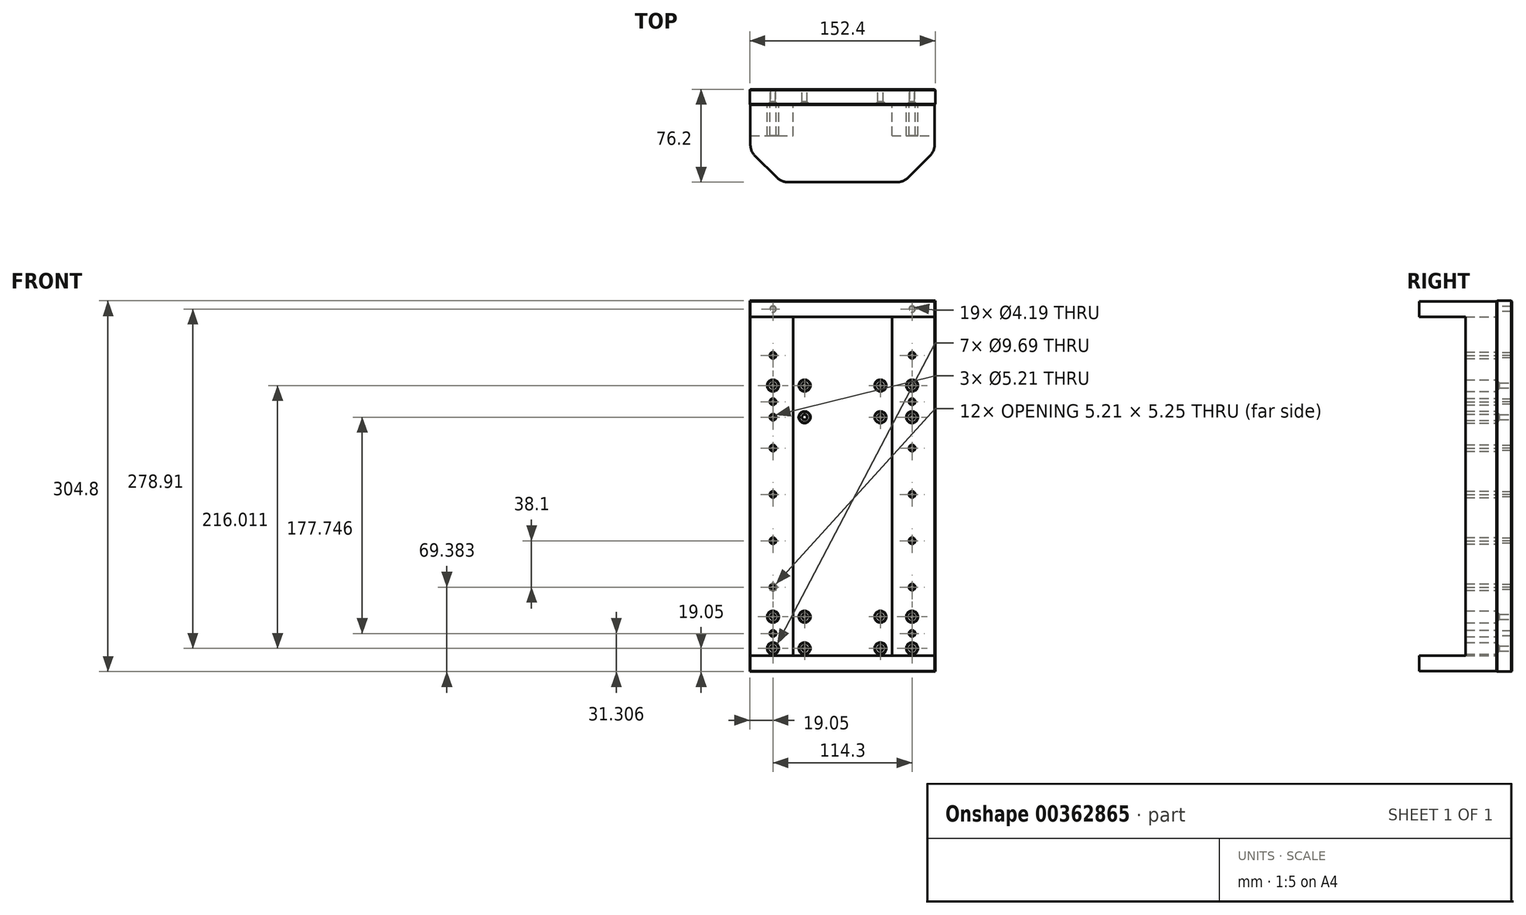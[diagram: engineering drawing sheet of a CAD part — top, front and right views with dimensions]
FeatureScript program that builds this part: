
annotation { "Feature Type Name" : "Feature", "Feature Type Description" : "" }
export const myFeature = defineFeature(function(context is Context, id is Id, definition is map)
    precondition{}
    {
        {
            var Q0;
            Q0=qCreatedBy(makeId("Front.planeOp"),FACE);
            var sketch = newSketch(context, id + "F0", { "sketchPlane" : qUnion([Q0])});
            skLineSegment(sketch, "E0.top", {"start": v(76.2, 152.4) * mm, "end": v(-76.2, 152.4) * mm});
            skLineSegment(sketch, "E0.left", {"start": v(76.2, -152.4) * mm, "end": v(76.2, 152.4) * mm});
            skLineSegment(sketch, "E0.right", {"start": v(-76.2, -152.4) * mm, "end": v(-76.2, 152.4) * mm});
            skPoint(sketch, "E0.middle", {"position": v(0, 0) * mm});
            skCircle(sketch, "E1.MirrorC", {"center": v(31.15, -107.35) * mm, "radius": 2.1 * mm});
            skCircle(sketch, "E2.MirrorC", {"center": v(57.15, -133.35) * mm, "radius": 2.1 * mm});
            skCircle(sketch, "E3.MirrorC", {"center": v(57.15, -107.35) * mm, "radius": 2.1 * mm});
            skCircle(sketch, "E4.MirrorC", {"center": v(31.15, -133.35) * mm, "radius": 2.1 * mm});
            skCircle(sketch, "E5.MirrorC", {"center": v(31.15, 82.66) * mm, "radius": 2.1 * mm});
            skCircle(sketch, "E6.MirrorC", {"center": v(57.15, 56.65) * mm, "radius": 2.1 * mm});
            skCircle(sketch, "E7.MirrorC", {"center": v(57.15, 82.66) * mm, "radius": 2.1 * mm});
            skCircle(sketch, "E8.MirrorC", {"center": v(31.15, 56.65) * mm, "radius": 2.1 * mm});
            skCircle(sketch, "E9.MirrorC", {"center": v(-57.15, -107.35) * mm, "radius": 2.1 * mm});
            skCircle(sketch, "E10.MirrorC", {"center": v(-31.15, -133.35) * mm, "radius": 2.1 * mm});
            skCircle(sketch, "E11.MirrorC", {"center": v(-31.15, -107.35) * mm, "radius": 2.1 * mm});
            skCircle(sketch, "E12.MirrorC", {"center": v(-57.15, -133.35) * mm, "radius": 2.1 * mm});
            skCircle(sketch, "E13.MirrorC", {"center": v(-57.15, 56.65) * mm, "radius": 2.1 * mm});
            skCircle(sketch, "E14.MirrorC", {"center": v(-31.14, 56.65) * mm, "radius": 2.1 * mm});
            skCircle(sketch, "E15.MirrorC", {"center": v(-31.15, 56.65) * mm, "radius": 2.1 * mm});
            skCircle(sketch, "E16.MirrorC", {"center": v(-57.15, 82.66) * mm, "radius": 2.1 * mm});
            skCircle(sketch, "E17.MirrorC", {"center": v(-31.15, 82.66) * mm, "radius": 2.1 * mm});
            skLineSegment(sketch, "E18", {"start": v(-76.2, -152.4) * mm, "end": v(76.2, -152.4) * mm});
            skLineSegment(sketch, "E19", {"start": v(-57.15, -133.35) * mm, "end": v(-57.15, -107.35) * mm, "construction": true});
            skLineSegment(sketch, "E20", {"start": v(-57.15, -120.35) * mm, "end": v(-69.56, -120.35) * mm, "construction": true});
            skPoint(sketch, "E20.endSnap0", {"position": v(-57.15, -120.35) * mm});
            skLineSegment(sketch, "E21", {"start": v(-69.56, -112.82) * mm, "end": v(-69.56, -127.88) * mm, "construction": true});
            skLineSegment(sketch, "E22", {"start": v(-63.35, -120.35) * mm, "end": v(-63.35, 68.86) * mm, "construction": true});
            skSolve(sketch);
        }
        {
            var Q0;
            Q0 = qSketchRegion(id + "F0", true);
            extrude(context, id + "F1", {"entities" : qUnion([Q0]), "depth" : 12.7 * mm});
        }
        {
            var Q0;
            Q0=makeQuery(id+"F1.opExtrude","CAP_EDGE",EDGE,{"disambiguationData":[OSD([sQuery(id+"F0.wireOp",EDGE,"E16.MirrorC")])],"isStart":false});
            var Q1;
            Q1=makeQuery(id+"F1.opExtrude","CAP_EDGE",EDGE,{"disambiguationData":[OSD([sQuery(id+"F0.wireOp",EDGE,"E17.MirrorC")])],"isStart":false});
            var Q2;
            Q2=makeQuery(id+"F1.opExtrude","CAP_EDGE",EDGE,{"disambiguationData":[OSD([sQuery(id+"F0.wireOp",EDGE,"E13.MirrorC")])],"isStart":false});
            var Q3;
            Q3=makeQuery(id+"F1.opExtrude","CAP_EDGE",EDGE,{"disambiguationData":[OSD([sQuery(id+"F0.wireOp",EDGE,"E15.MirrorC")])],"isStart":false});
            var Q4;
            Q4=makeQuery(id+"F1.opExtrude","CAP_EDGE",EDGE,{"disambiguationData":[OSD([sQuery(id+"F0.wireOp",EDGE,"E5.MirrorC")])],"isStart":false});
            var Q5;
            Q5=makeQuery(id+"F1.opExtrude","CAP_EDGE",EDGE,{"disambiguationData":[OSD([sQuery(id+"F0.wireOp",EDGE,"E7.MirrorC")])],"isStart":false});
            var Q6;
            Q6=makeQuery(id+"F1.opExtrude","CAP_EDGE",EDGE,{"disambiguationData":[OSD([sQuery(id+"F0.wireOp",EDGE,"E8.MirrorC")])],"isStart":false});
            var Q7;
            Q7=makeQuery(id+"F1.opExtrude","CAP_EDGE",EDGE,{"disambiguationData":[OSD([sQuery(id+"F0.wireOp",EDGE,"E6.MirrorC")])],"isStart":false});
            var Q8;
            Q8=makeQuery(id+"F1.opExtrude","CAP_EDGE",EDGE,{"disambiguationData":[OSD([sQuery(id+"F0.wireOp",EDGE,"E9.MirrorC")])],"isStart":false});
            var Q9;
            Q9=makeQuery(id+"F1.opExtrude","CAP_EDGE",EDGE,{"disambiguationData":[OSD([sQuery(id+"F0.wireOp",EDGE,"E11.MirrorC")])],"isStart":false});
            var Q10;
            Q10=makeQuery(id+"F1.opExtrude","CAP_EDGE",EDGE,{"disambiguationData":[OSD([sQuery(id+"F0.wireOp",EDGE,"E1.MirrorC")])],"isStart":false});
            var Q11;
            Q11=makeQuery(id+"F1.opExtrude","CAP_EDGE",EDGE,{"disambiguationData":[OSD([sQuery(id+"F0.wireOp",EDGE,"E3.MirrorC")])],"isStart":false});
            var Q12;
            Q12=makeQuery(id+"F1.opExtrude","CAP_EDGE",EDGE,{"disambiguationData":[OSD([sQuery(id+"F0.wireOp",EDGE,"E12.MirrorC")])],"isStart":false});
            var Q13;
            Q13=makeQuery(id+"F1.opExtrude","CAP_EDGE",EDGE,{"disambiguationData":[OSD([sQuery(id+"F0.wireOp",EDGE,"E10.MirrorC")])],"isStart":false});
            var Q14;
            Q14=makeQuery(id+"F1.opExtrude","CAP_EDGE",EDGE,{"disambiguationData":[OSD([sQuery(id+"F0.wireOp",EDGE,"E4.MirrorC")])],"isStart":false});
            var Q15;
            Q15=makeQuery(id+"F1.opExtrude","CAP_EDGE",EDGE,{"disambiguationData":[OSD([sQuery(id+"F0.wireOp",EDGE,"E2.MirrorC")])],"isStart":false});
            chamfer(context, id + "F2", {"entities" : qUnion([Q0, Q1, Q2, Q3, Q4, Q5, Q6, Q7, Q8, Q9, Q10, Q11, Q12, Q13, Q14, Q15]), "width" : 2.54 * mm, "tangentPropagation" : true});
        }
        {
            var Q0;
            Q0=makeQuery(id+"F1.opExtrude","CAP_FACE",FACE,{"disambiguationData":[OSD([sQuery(id+"F0.wireOp",EDGE,"E0.bottom"),sQuery(id+"F0.wireOp",EDGE,"E0.top"),sQuery(id+"F0.wireOp",EDGE,"E0.left"),sQuery(id+"F0.wireOp",EDGE,"E0.right"),sQuery(id+"F0.wireOp",EDGE,"E1.MirrorC"),sQuery(id+"F0.wireOp",EDGE,"E2.MirrorC"),sQuery(id+"F0.wireOp",EDGE,"E3.MirrorC"),sQuery(id+"F0.wireOp",EDGE,"E4.MirrorC"),sQuery(id+"F0.wireOp",EDGE,"E5.MirrorC"),sQuery(id+"F0.wireOp",EDGE,"E6.MirrorC"),sQuery(id+"F0.wireOp",EDGE,"E7.MirrorC"),sQuery(id+"F0.wireOp",EDGE,"E8.MirrorC"),sQuery(id+"F0.wireOp",EDGE,"E9.MirrorC"),sQuery(id+"F0.wireOp",EDGE,"E10.MirrorC"),sQuery(id+"F0.wireOp",EDGE,"E11.MirrorC"),sQuery(id+"F0.wireOp",EDGE,"E12.MirrorC"),sQuery(id+"F0.wireOp",EDGE,"E15.MirrorC"),sQuery(id+"F0.wireOp",EDGE,"E13.MirrorC"),sQuery(id+"F0.wireOp",EDGE,"E16.MirrorC"),sQuery(id+"F0.wireOp",EDGE,"E17.MirrorC")])],"isStart":false});
            var sketch = newSketch(context, id + "F3", { "sketchPlane" : qUnion([Q0])});
            skCircle(sketch, "E23", {"center": v(-57.15, -83.04) * mm, "radius": 2.1 * mm});
            skCircle(sketch, "E24.0.1.0", {"center": v(-57.15, -44.94) * mm, "radius": 2.1 * mm});
            skLineSegment(sketch, "E24.direction1", {"start": v(-57.15, -83.04) * mm, "end": v(57.15, -83.04) * mm, "construction": true});
            skLineSegment(sketch, "E24.direction2", {"start": v(-57.15, -83.04) * mm, "end": v(-57.15, -44.94) * mm, "construction": true});
            skCircle(sketch, "E25.0.0.2", {"center": v(-57.15, -6.84) * mm, "radius": 2.1 * mm});
            skCircle(sketch, "E25.0.0.3", {"center": v(-57.15, 31.26) * mm, "radius": 2.1 * mm});
            skCircle(sketch, "E25.0.0.4", {"center": v(-57.15, 69.36) * mm, "radius": 2.1 * mm});
            skCircle(sketch, "E25.0.0.5", {"center": v(-57.15, 107.46) * mm, "radius": 2.1 * mm});
            skCircle(sketch, "E25.0.0.6", {"center": v(-57.15, 145.56) * mm, "radius": 2.1 * mm});
            skCircle(sketch, "E26.0.1.0", {"center": v(57.15, -83.04) * mm, "radius": 2.1 * mm});
            skCircle(sketch, "E26.0.1.1", {"center": v(57.15, -44.94) * mm, "radius": 2.1 * mm});
            skCircle(sketch, "E26.0.1.2", {"center": v(57.15, -6.84) * mm, "radius": 2.1 * mm});
            skCircle(sketch, "E26.0.1.3", {"center": v(57.15, 31.26) * mm, "radius": 2.1 * mm});
            skCircle(sketch, "E26.0.1.4", {"center": v(57.15, 69.36) * mm, "radius": 2.1 * mm});
            skCircle(sketch, "E26.0.1.5", {"center": v(57.15, 107.46) * mm, "radius": 2.1 * mm});
            skCircle(sketch, "E26.0.1.6", {"center": v(57.15, 145.56) * mm, "radius": 2.1 * mm});
            skCircle(sketch, "E27", {"center": v(-57.15, -121.1) * mm, "radius": 2.1 * mm});
            skCircle(sketch, "E28.0.1.0", {"center": v(-57.15, -83) * mm, "radius": 2.1 * mm});
            skLineSegment(sketch, "E28.direction1", {"start": v(-57.15, -121.1) * mm, "end": v(57.15, -121.1) * mm, "construction": true});
            skLineSegment(sketch, "E28.direction2", {"start": v(-57.15, -121.1) * mm, "end": v(-57.15, -83) * mm, "construction": true});
            skCircle(sketch, "E29.0.0.2", {"center": v(-57.15, -44.9) * mm, "radius": 2.1 * mm});
            skCircle(sketch, "E29.0.0.3", {"center": v(-57.15, -6.8) * mm, "radius": 2.1 * mm});
            skCircle(sketch, "E29.0.0.4", {"center": v(-57.15, 31.3) * mm, "radius": 2.1 * mm});
            skCircle(sketch, "E29.0.0.5", {"center": v(-57.15, 69.4) * mm, "radius": 2.1 * mm});
            skCircle(sketch, "E29.0.0.6", {"center": v(-57.15, 107.5) * mm, "radius": 2.1 * mm});
            skCircle(sketch, "E30.0.1.0", {"center": v(57.15, -121.1) * mm, "radius": 2.1 * mm});
            skCircle(sketch, "E30.0.1.1", {"center": v(57.15, -83) * mm, "radius": 2.1 * mm});
            skCircle(sketch, "E30.0.1.2", {"center": v(57.15, -44.9) * mm, "radius": 2.1 * mm});
            skCircle(sketch, "E30.0.1.3", {"center": v(57.15, -6.8) * mm, "radius": 2.1 * mm});
            skCircle(sketch, "E30.0.1.4", {"center": v(57.15, 31.3) * mm, "radius": 2.1 * mm});
            skCircle(sketch, "E30.0.1.5", {"center": v(57.15, 69.4) * mm, "radius": 2.1 * mm});
            skCircle(sketch, "E30.0.1.6", {"center": v(57.15, 107.5) * mm, "radius": 2.1 * mm});
            skSolve(sketch);
        }
        {
            var Q0;
            Q0 = qSketchRegion(id + "F3", true);
            extrude(context, id + "F4", {"entities" : qUnion([Q0]), "operationType" : NewBodyOperationType.REMOVE, "oppositeDirection" : true, "depth" : 25.4 * mm});
        }
        {
            var Q0;
            Q0=makeQuery(id+"F1.opExtrude","CAP_FACE",FACE,{"disambiguationData":[OSD([sQuery(id+"F0.wireOp",EDGE,"E0.top"),sQuery(id+"F0.wireOp",EDGE,"E0.left"),sQuery(id+"F0.wireOp",EDGE,"E0.right"),sQuery(id+"F0.wireOp",EDGE,"E1.MirrorC"),sQuery(id+"F0.wireOp",EDGE,"E2.MirrorC"),sQuery(id+"F0.wireOp",EDGE,"E3.MirrorC"),sQuery(id+"F0.wireOp",EDGE,"E4.MirrorC"),sQuery(id+"F0.wireOp",EDGE,"E5.MirrorC"),sQuery(id+"F0.wireOp",EDGE,"E6.MirrorC"),sQuery(id+"F0.wireOp",EDGE,"E7.MirrorC"),sQuery(id+"F0.wireOp",EDGE,"E8.MirrorC"),sQuery(id+"F0.wireOp",EDGE,"E9.MirrorC"),sQuery(id+"F0.wireOp",EDGE,"E10.MirrorC"),sQuery(id+"F0.wireOp",EDGE,"E11.MirrorC"),sQuery(id+"F0.wireOp",EDGE,"E12.MirrorC"),sQuery(id+"F0.wireOp",EDGE,"E14.MirrorC"),sQuery(id+"F0.wireOp",EDGE,"E15.MirrorC"),sQuery(id+"F0.wireOp",EDGE,"E13.MirrorC"),sQuery(id+"F0.wireOp",EDGE,"E16.MirrorC"),sQuery(id+"F0.wireOp",EDGE,"E17.MirrorC"),sQuery(id+"F0.wireOp",EDGE,"E18")])],"isStart":false});
            chamfer(context, id + "F5", {"entities" : qUnion([Q0]), "width" : 0.5 * mm, "tangentPropagation" : true});
        }
        {
            var Q0;
            Q0=makeQuery(id+"F1.opExtrude","CAP_FACE",FACE,{"disambiguationData":[OSD([sQuery(id+"F0.wireOp",EDGE,"E0.top"),sQuery(id+"F0.wireOp",EDGE,"E0.left"),sQuery(id+"F0.wireOp",EDGE,"E0.right"),sQuery(id+"F0.wireOp",EDGE,"E1.MirrorC"),sQuery(id+"F0.wireOp",EDGE,"E2.MirrorC"),sQuery(id+"F0.wireOp",EDGE,"E3.MirrorC"),sQuery(id+"F0.wireOp",EDGE,"E4.MirrorC"),sQuery(id+"F0.wireOp",EDGE,"E5.MirrorC"),sQuery(id+"F0.wireOp",EDGE,"E6.MirrorC"),sQuery(id+"F0.wireOp",EDGE,"E7.MirrorC"),sQuery(id+"F0.wireOp",EDGE,"E8.MirrorC"),sQuery(id+"F0.wireOp",EDGE,"E9.MirrorC"),sQuery(id+"F0.wireOp",EDGE,"E10.MirrorC"),sQuery(id+"F0.wireOp",EDGE,"E11.MirrorC"),sQuery(id+"F0.wireOp",EDGE,"E12.MirrorC"),sQuery(id+"F0.wireOp",EDGE,"E14.MirrorC"),sQuery(id+"F0.wireOp",EDGE,"E15.MirrorC"),sQuery(id+"F0.wireOp",EDGE,"E13.MirrorC"),sQuery(id+"F0.wireOp",EDGE,"E16.MirrorC"),sQuery(id+"F0.wireOp",EDGE,"E17.MirrorC"),sQuery(id+"F0.wireOp",EDGE,"E18")])],"isStart":true});
            chamfer(context, id + "F6", {"entities" : qUnion([Q0]), "width" : 0.5 * mm, "tangentPropagation" : true});
        }
        {
            var Q0;
            Q0=makeQuery(id+"F1.opExtrude","CAP_FACE",FACE,{"disambiguationData":[OSD([sQuery(id+"F0.wireOp",EDGE,"E0.top"),sQuery(id+"F0.wireOp",EDGE,"E0.left"),sQuery(id+"F0.wireOp",EDGE,"E0.right"),sQuery(id+"F0.wireOp",EDGE,"E1.MirrorC"),sQuery(id+"F0.wireOp",EDGE,"E2.MirrorC"),sQuery(id+"F0.wireOp",EDGE,"E3.MirrorC"),sQuery(id+"F0.wireOp",EDGE,"E4.MirrorC"),sQuery(id+"F0.wireOp",EDGE,"E5.MirrorC"),sQuery(id+"F0.wireOp",EDGE,"E6.MirrorC"),sQuery(id+"F0.wireOp",EDGE,"E7.MirrorC"),sQuery(id+"F0.wireOp",EDGE,"E8.MirrorC"),sQuery(id+"F0.wireOp",EDGE,"E9.MirrorC"),sQuery(id+"F0.wireOp",EDGE,"E10.MirrorC"),sQuery(id+"F0.wireOp",EDGE,"E11.MirrorC"),sQuery(id+"F0.wireOp",EDGE,"E12.MirrorC"),sQuery(id+"F0.wireOp",EDGE,"E14.MirrorC"),sQuery(id+"F0.wireOp",EDGE,"E15.MirrorC"),sQuery(id+"F0.wireOp",EDGE,"E13.MirrorC"),sQuery(id+"F0.wireOp",EDGE,"E16.MirrorC"),sQuery(id+"F0.wireOp",EDGE,"E17.MirrorC"),sQuery(id+"F0.wireOp",EDGE,"E18")])],"isStart":false});
            var sketch = newSketch(context, id + "F7", { "sketchPlane" : qUnion([Q0])});
            skLineSegment(sketch, "E31.bottom", {"start": v(-75.7, 151.9) * mm, "end": v(75.7, 151.9) * mm});
            skLineSegment(sketch, "E31.top", {"start": v(-75.7, 139.2) * mm, "end": v(75.7, 139.2) * mm});
            skLineSegment(sketch, "E31.left", {"start": v(-75.7, 151.9) * mm, "end": v(-75.7, 139.2) * mm});
            skLineSegment(sketch, "E31.right", {"start": v(75.7, 151.9) * mm, "end": v(75.7, 139.2) * mm});
            skSolve(sketch);
        }
        {
            var Q0;
            Q0 = qSketchRegion(id + "F7", true);
            extrude(context, id + "F8", {"entities" : qUnion([Q0]), "depth" : 63.5 * mm});
        }
        {
            var Q0;
            Q0=makeQuery(id+"F8.opExtrude","SWEPT_BODY",BODY,{"disambiguationData":[OSD([sQuery(id+"F7.wireOp",EDGE,"E31.bottom"),sQuery(id+"F7.wireOp",EDGE,"E31.top"),sQuery(id+"F7.wireOp",EDGE,"E31.left"),sQuery(id+"F7.wireOp",EDGE,"E31.right")])]});
            var Q1;
            Q1=qCreatedBy(makeId("Top.planeOp"),FACE);
            mirror(context, id + "F9", {"operationType" : NewBodyOperationType.ADD, "entities" : qUnion([Q0]), "mirrorPlane" : qUnion([Q1])});
        }
        {
            var Q0;
            Q0=makeQuery(id+"F8.opExtrude","CAP_EDGE",EDGE,{"disambiguationData":[OSD([sQuery(id+"F7.wireOp",EDGE,"E31.left")])],"isStart":false});
            var Q1;
            Q1=makeQuery(id+"F8.opExtrude","CAP_EDGE",EDGE,{"disambiguationData":[OSD([sQuery(id+"F7.wireOp",EDGE,"E31.right")])],"isStart":false});
            var Q2;
            Q2=makeQuery(id+"F9.opPattern","COPY",EDGE,{"derivedFrom":makeQuery(id+"F8.opExtrude","CAP_EDGE",EDGE,{"disambiguationData":[OSD([sQuery(id+"F7.wireOp",EDGE,"E31.left")])],"isStart":false}),"instanceName":"1"});
            var Q3;
            Q3=makeQuery(id+"F9.opPattern","COPY",EDGE,{"derivedFrom":makeQuery(id+"F8.opExtrude","CAP_EDGE",EDGE,{"disambiguationData":[OSD([sQuery(id+"F7.wireOp",EDGE,"E31.right")])],"isStart":false}),"instanceName":"1"});
            chamfer(context, id + "F10", {"entities" : qUnion([Q0, Q1, Q2, Q3]), "width" : 25.4 * mm, "tangentPropagation" : true});
        }
        {
            var Q0;
            {var subQ0=sQuery(id+"F7.wireOp",EDGE,"E31.left");Q0=makeQuery(id+"F10.opChamfer","BLEND_EDGE",EDGE,{"blendedFrom":[makeQuery(id+"F9.opPattern","COPY",EDGE,{"derivedFrom":makeQuery(id+"F8.opExtrude","CAP_EDGE",EDGE,{"disambiguationData":[OSD([subQ0])],"isStart":false}),"instanceName":"1"}),makeQuery(id+"F9.opPattern","COPY",FACE,{"derivedFrom":makeQuery(id+"F8.opExtrude","CAP_FACE",FACE,{"disambiguationData":[OSD([sQuery(id+"F7.wireOp",EDGE,"E31.bottom"),sQuery(id+"F7.wireOp",EDGE,"E31.top"),subQ0,sQuery(id+"F7.wireOp",EDGE,"E31.right")])],"isStart":false}),"instanceName":"1"})],"blendedInto":[makeQuery(id+"F9.opPattern","COPY",FACE,{"derivedFrom":makeQuery(id+"F8.opExtrude","CAP_FACE",FACE,{"disambiguationData":[OSD([sQuery(id+"F7.wireOp",EDGE,"E31.bottom"),sQuery(id+"F7.wireOp",EDGE,"E31.top"),subQ0,sQuery(id+"F7.wireOp",EDGE,"E31.right")])],"isStart":false}),"instanceName":"1"})]});}
            var Q1;
            {var subQ0=sQuery(id+"F7.wireOp",EDGE,"E31.left");Q1=makeQuery(id+"F10.opChamfer","BLEND_EDGE",EDGE,{"blendedFrom":[makeQuery(id+"F9.opPattern","COPY",EDGE,{"derivedFrom":makeQuery(id+"F8.opExtrude","CAP_EDGE",EDGE,{"disambiguationData":[OSD([subQ0])],"isStart":false}),"instanceName":"1"}),makeQuery(id+"F9.opPattern","COPY",FACE,{"derivedFrom":makeQuery(id+"F8.opExtrude","SWEPT_FACE",FACE,{"disambiguationData":[OSD([subQ0])]}),"instanceName":"1"})],"blendedInto":[makeQuery(id+"F9.opPattern","COPY",FACE,{"derivedFrom":makeQuery(id+"F8.opExtrude","SWEPT_FACE",FACE,{"disambiguationData":[OSD([subQ0])]}),"instanceName":"1"})]});}
            var Q2;
            {var subQ0=sQuery(id+"F7.wireOp",EDGE,"E31.right");Q2=makeQuery(id+"F10.opChamfer","BLEND_EDGE",EDGE,{"blendedFrom":[makeQuery(id+"F9.opPattern","COPY",EDGE,{"derivedFrom":makeQuery(id+"F8.opExtrude","CAP_EDGE",EDGE,{"disambiguationData":[OSD([subQ0])],"isStart":false}),"instanceName":"1"}),makeQuery(id+"F9.opPattern","COPY",FACE,{"derivedFrom":makeQuery(id+"F8.opExtrude","CAP_FACE",FACE,{"disambiguationData":[OSD([sQuery(id+"F7.wireOp",EDGE,"E31.bottom"),sQuery(id+"F7.wireOp",EDGE,"E31.top"),sQuery(id+"F7.wireOp",EDGE,"E31.left"),subQ0])],"isStart":false}),"instanceName":"1"})],"blendedInto":[makeQuery(id+"F9.opPattern","COPY",FACE,{"derivedFrom":makeQuery(id+"F8.opExtrude","CAP_FACE",FACE,{"disambiguationData":[OSD([sQuery(id+"F7.wireOp",EDGE,"E31.bottom"),sQuery(id+"F7.wireOp",EDGE,"E31.top"),sQuery(id+"F7.wireOp",EDGE,"E31.left"),subQ0])],"isStart":false}),"instanceName":"1"})]});}
            var Q3;
            {var subQ0=sQuery(id+"F7.wireOp",EDGE,"E31.right");Q3=makeQuery(id+"F10.opChamfer","BLEND_EDGE",EDGE,{"blendedFrom":[makeQuery(id+"F9.opPattern","COPY",EDGE,{"derivedFrom":makeQuery(id+"F8.opExtrude","CAP_EDGE",EDGE,{"disambiguationData":[OSD([subQ0])],"isStart":false}),"instanceName":"1"}),makeQuery(id+"F9.opPattern","COPY",FACE,{"derivedFrom":makeQuery(id+"F8.opExtrude","SWEPT_FACE",FACE,{"disambiguationData":[OSD([subQ0])]}),"instanceName":"1"})],"blendedInto":[makeQuery(id+"F9.opPattern","COPY",FACE,{"derivedFrom":makeQuery(id+"F8.opExtrude","SWEPT_FACE",FACE,{"disambiguationData":[OSD([subQ0])]}),"instanceName":"1"})]});}
            var Q4;
            {var subQ0=sQuery(id+"F7.wireOp",EDGE,"E31.left");Q4=makeQuery(id+"F10.opChamfer","BLEND_EDGE",EDGE,{"blendedFrom":[makeQuery(id+"F8.opExtrude","CAP_EDGE",EDGE,{"disambiguationData":[OSD([subQ0])],"isStart":false}),makeQuery(id+"F8.opExtrude","SWEPT_FACE",FACE,{"disambiguationData":[OSD([subQ0])]})],"blendedInto":[makeQuery(id+"F8.opExtrude","SWEPT_FACE",FACE,{"disambiguationData":[OSD([subQ0])]})]});}
            var Q5;
            {var subQ0=sQuery(id+"F7.wireOp",EDGE,"E31.left");Q5=makeQuery(id+"F10.opChamfer","BLEND_EDGE",EDGE,{"blendedFrom":[makeQuery(id+"F8.opExtrude","CAP_EDGE",EDGE,{"disambiguationData":[OSD([subQ0])],"isStart":false}),makeQuery(id+"F8.opExtrude","CAP_FACE",FACE,{"disambiguationData":[OSD([sQuery(id+"F7.wireOp",EDGE,"E31.bottom"),sQuery(id+"F7.wireOp",EDGE,"E31.top"),subQ0,sQuery(id+"F7.wireOp",EDGE,"E31.right")])],"isStart":false})],"blendedInto":[makeQuery(id+"F8.opExtrude","CAP_FACE",FACE,{"disambiguationData":[OSD([sQuery(id+"F7.wireOp",EDGE,"E31.bottom"),sQuery(id+"F7.wireOp",EDGE,"E31.top"),subQ0,sQuery(id+"F7.wireOp",EDGE,"E31.right")])],"isStart":false})]});}
            var Q6;
            {var subQ0=sQuery(id+"F7.wireOp",EDGE,"E31.right");Q6=makeQuery(id+"F10.opChamfer","BLEND_EDGE",EDGE,{"blendedFrom":[makeQuery(id+"F8.opExtrude","CAP_EDGE",EDGE,{"disambiguationData":[OSD([subQ0])],"isStart":false}),makeQuery(id+"F8.opExtrude","CAP_FACE",FACE,{"disambiguationData":[OSD([sQuery(id+"F7.wireOp",EDGE,"E31.bottom"),sQuery(id+"F7.wireOp",EDGE,"E31.top"),sQuery(id+"F7.wireOp",EDGE,"E31.left"),subQ0])],"isStart":false})],"blendedInto":[makeQuery(id+"F8.opExtrude","CAP_FACE",FACE,{"disambiguationData":[OSD([sQuery(id+"F7.wireOp",EDGE,"E31.bottom"),sQuery(id+"F7.wireOp",EDGE,"E31.top"),sQuery(id+"F7.wireOp",EDGE,"E31.left"),subQ0])],"isStart":false})]});}
            var Q7;
            {var subQ0=sQuery(id+"F7.wireOp",EDGE,"E31.right");Q7=makeQuery(id+"F10.opChamfer","BLEND_EDGE",EDGE,{"blendedFrom":[makeQuery(id+"F8.opExtrude","CAP_EDGE",EDGE,{"disambiguationData":[OSD([subQ0])],"isStart":false}),makeQuery(id+"F8.opExtrude","SWEPT_FACE",FACE,{"disambiguationData":[OSD([subQ0])]})],"blendedInto":[makeQuery(id+"F8.opExtrude","SWEPT_FACE",FACE,{"disambiguationData":[OSD([subQ0])]})]});}
            fillet(context, id + "F11", {"entities" : qUnion([Q0, Q1, Q2, Q3, Q4, Q5, Q6, Q7]), "radius" : 12.7 * mm, "tangentPropagation" : true, "allowEdgeOverflow" : false});
        }
        {
            var Q0;
            Q0=makeQuery(id+"F1.opExtrude","CAP_FACE",FACE,{"disambiguationData":[OSD([sQuery(id+"F0.wireOp",EDGE,"E0.top"),sQuery(id+"F0.wireOp",EDGE,"E0.left"),sQuery(id+"F0.wireOp",EDGE,"E0.right"),sQuery(id+"F0.wireOp",EDGE,"E1.MirrorC"),sQuery(id+"F0.wireOp",EDGE,"E2.MirrorC"),sQuery(id+"F0.wireOp",EDGE,"E3.MirrorC"),sQuery(id+"F0.wireOp",EDGE,"E4.MirrorC"),sQuery(id+"F0.wireOp",EDGE,"E5.MirrorC"),sQuery(id+"F0.wireOp",EDGE,"E6.MirrorC"),sQuery(id+"F0.wireOp",EDGE,"E7.MirrorC"),sQuery(id+"F0.wireOp",EDGE,"E8.MirrorC"),sQuery(id+"F0.wireOp",EDGE,"E9.MirrorC"),sQuery(id+"F0.wireOp",EDGE,"E10.MirrorC"),sQuery(id+"F0.wireOp",EDGE,"E11.MirrorC"),sQuery(id+"F0.wireOp",EDGE,"E12.MirrorC"),sQuery(id+"F0.wireOp",EDGE,"E14.MirrorC"),sQuery(id+"F0.wireOp",EDGE,"E15.MirrorC"),sQuery(id+"F0.wireOp",EDGE,"E13.MirrorC"),sQuery(id+"F0.wireOp",EDGE,"E16.MirrorC"),sQuery(id+"F0.wireOp",EDGE,"E17.MirrorC"),sQuery(id+"F0.wireOp",EDGE,"E18")])],"isStart":false});
            var sketch = newSketch(context, id + "F12", { "sketchPlane" : qUnion([Q0])});
            skLineSegment(sketch, "E32.bottom", {"start": v(-75.7, 139.2) * mm, "end": v(-40.64, 139.2) * mm});
            skLineSegment(sketch, "E32.top", {"start": v(-75.7, -139.2) * mm, "end": v(-40.64, -139.2) * mm});
            skLineSegment(sketch, "E32.left", {"start": v(-75.7, 139.2) * mm, "end": v(-75.7, -139.2) * mm});
            skLineSegment(sketch, "E32.right", {"start": v(-40.64, 139.2) * mm, "end": v(-40.64, -139.2) * mm});
            skLineSegment(sketch, "E33.MirrorCS", {"start": v(40.64, 139.2) * mm, "end": v(40.64, -139.2) * mm});
            skSolve(sketch);
        }
        {
            var Q0;
            {var subQ7=sQuery(id+"F12.wireOp",EDGE,"E33.MirrorCS");Q0=makeQuery(id+"F12.imprint","IMPRINT",FACE,{"disambiguationData":[TD([[makeQuery(id+"F12.imprint","IMPRINT",EDGE,{"derivedFrom":subQ7}),1.0]])]});}
            var Q1;
            Q1=makeQuery(id+"F12.imprint","IMPRINT",FACE,{"disambiguationData":[TD([[makeQuery(id+"F12.imprint","IMPRINT",EDGE,{"derivedFrom":sQuery(id+"F12.wireOp",EDGE,"E32.bottom")}),-1.0]])]});
            extrude(context, id + "F13", {"entities" : qUnion([Q0, Q1]), "operationType" : NewBodyOperationType.ADD, "depth" : 25.4 * mm});
        }
    });
